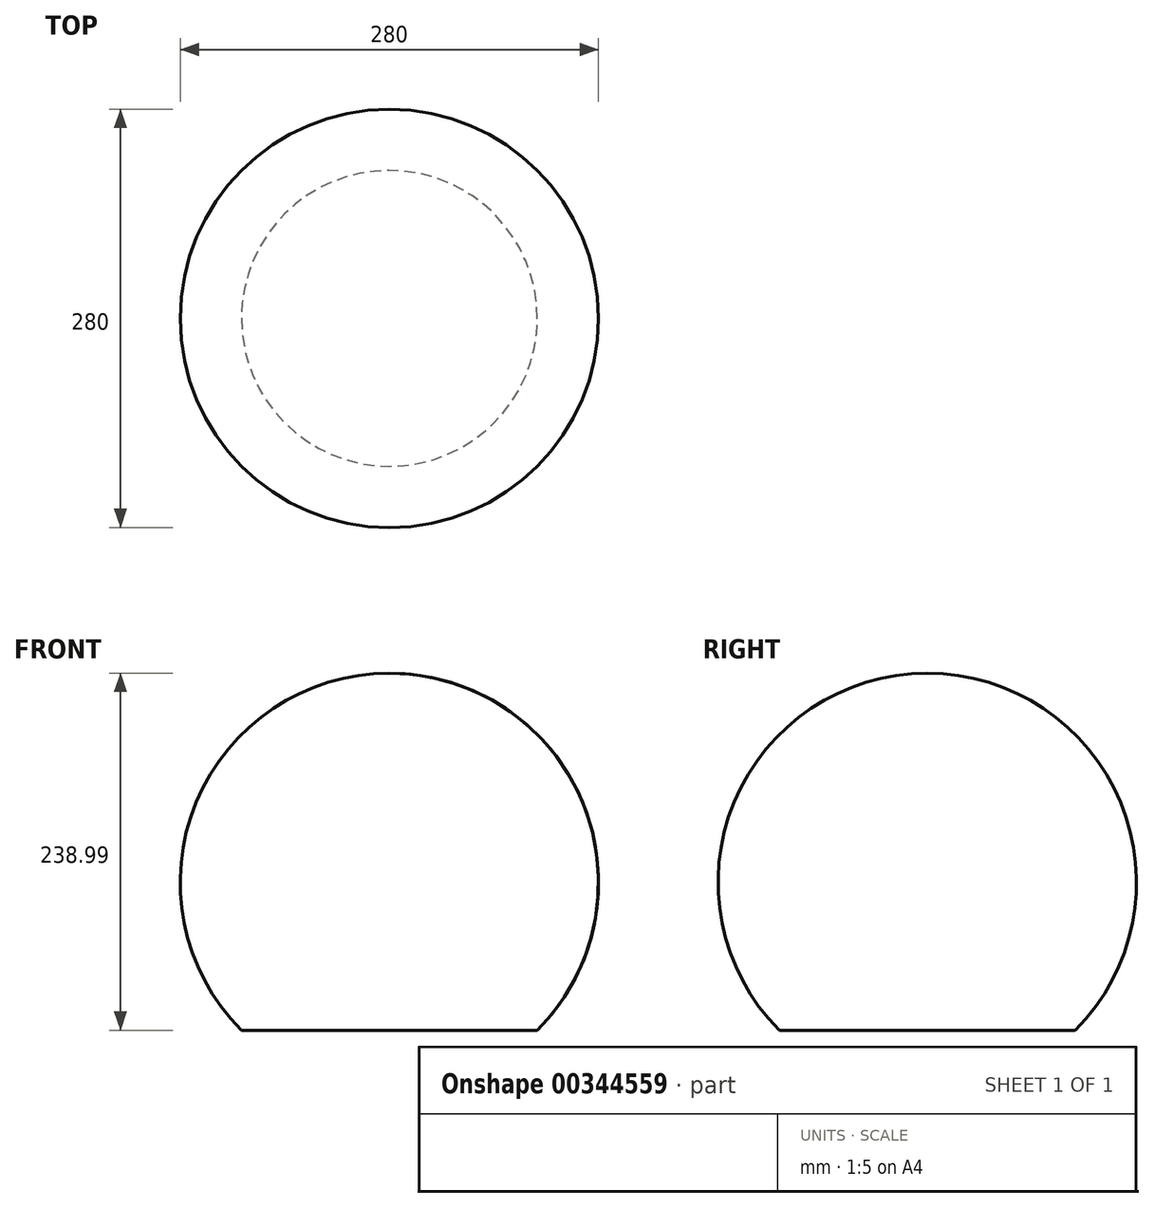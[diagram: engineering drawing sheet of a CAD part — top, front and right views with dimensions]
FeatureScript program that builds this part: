
annotation { "Feature Type Name" : "Feature", "Feature Type Description" : "" }
export const myFeature = defineFeature(function(context is Context, id is Id, definition is map)
    precondition{}
    {
        {
            var Q0;
            Q0=qCreatedBy(makeId("Top.planeOp"),FACE);
            var sketch = newSketch(context, id + "F0", { "sketchPlane" : qUnion([Q0])});
            skCircle(sketch, "E0", {"center": v(0, 0) * mm, "radius": 40.75 * mm});
            skLineSegment(sketch, "E1.bottom", {"start": v(6.25, -45.1) * mm, "end": v(-6.25, -45.1) * mm});
            skLineSegment(sketch, "E1.top", {"start": v(7.25, -40.1) * mm, "end": v(-7.25, -40.1) * mm});
            skLineSegment(sketch, "E1.left", {"start": v(7.25, -44.1) * mm, "end": v(7.25, -40.1) * mm});
            skLineSegment(sketch, "E1.right", {"start": v(-7.25, -44.1) * mm, "end": v(-7.25, -40.1) * mm});
            skPoint(sketch, "E1.middle", {"position": v(0, -42.6) * mm});
            skPoint(sketch, "E2.visualSharp", {"position": v(-7.25, -45.1) * mm});
            skArc(sketch, "E2.filletArc", {"start": v(-7.25, -44.1) * mm, "mid": v(-6.96, -44.8) * mm, "end": v(-6.25, -45.1) * mm});
            skPoint(sketch, "E3.visualSharp", {"position": v(7.25, -45.1) * mm});
            skArc(sketch, "E3.filletArc", {"start": v(6.25, -45.1) * mm, "mid": v(6.96, -44.8) * mm, "end": v(7.25, -44.1) * mm});
            skPoint(sketch, "E4.1.0", {"position": v(45.1, 7.25) * mm});
            skLineSegment(sketch, "E4.1.1", {"start": v(45.1, 6.25) * mm, "end": v(45.1, -6.25) * mm});
            skPoint(sketch, "E4.1.2", {"position": v(45.1, -7.25) * mm});
            skArc(sketch, "E4.1.3", {"start": v(44.1, -7.25) * mm, "mid": v(44.8, -6.96) * mm, "end": v(45.1, -6.25) * mm});
            skArc(sketch, "E4.1.4", {"start": v(45.1, 6.25) * mm, "mid": v(44.8, 6.96) * mm, "end": v(44.1, 7.25) * mm});
            skLineSegment(sketch, "E4.1.5", {"start": v(44.1, 7.25) * mm, "end": v(40.1, 7.25) * mm});
            skLineSegment(sketch, "E4.1.6", {"start": v(44.1, -7.25) * mm, "end": v(40.1, -7.25) * mm});
            skPoint(sketch, "E4.2.0", {"position": v(-7.25, 45.1) * mm});
            skLineSegment(sketch, "E4.2.1", {"start": v(-6.25, 45.1) * mm, "end": v(6.25, 45.1) * mm});
            skPoint(sketch, "E4.2.2", {"position": v(7.25, 45.1) * mm});
            skArc(sketch, "E4.2.3", {"start": v(7.25, 44.1) * mm, "mid": v(6.96, 44.8) * mm, "end": v(6.25, 45.1) * mm});
            skArc(sketch, "E4.2.4", {"start": v(-6.25, 45.1) * mm, "mid": v(-6.96, 44.8) * mm, "end": v(-7.25, 44.1) * mm});
            skLineSegment(sketch, "E4.2.5", {"start": v(-7.25, 44.1) * mm, "end": v(-7.25, 40.1) * mm});
            skLineSegment(sketch, "E4.2.6", {"start": v(7.25, 44.1) * mm, "end": v(7.25, 40.1) * mm});
            skPoint(sketch, "E4.3.0", {"position": v(-45.1, -7.25) * mm});
            skLineSegment(sketch, "E4.3.1", {"start": v(-45.1, -6.25) * mm, "end": v(-45.1, 6.25) * mm});
            skPoint(sketch, "E4.3.2", {"position": v(-45.1, 7.25) * mm});
            skArc(sketch, "E4.3.3", {"start": v(-44.1, 7.25) * mm, "mid": v(-44.8, 6.96) * mm, "end": v(-45.1, 6.25) * mm});
            skArc(sketch, "E4.3.4", {"start": v(-45.1, -6.25) * mm, "mid": v(-44.8, -6.96) * mm, "end": v(-44.1, -7.25) * mm});
            skLineSegment(sketch, "E4.3.5", {"start": v(-44.1, -7.25) * mm, "end": v(-40.1, -7.25) * mm});
            skLineSegment(sketch, "E4.3.6", {"start": v(-44.1, 7.25) * mm, "end": v(-40.1, 7.25) * mm});
            skSolve(sketch);
        }
        {
            var Q0;
            Q0=qCreatedBy(makeId("Front.planeOp"),FACE);
            var sketch = newSketch(context, id + "F1", { "sketchPlane" : qUnion([Q0])});
            skArc(sketch, "E5", {"start": v(99, 0) * mm, "mid": v(0, 239) * mm, "end": v(-99, 0) * mm});
            skLineSegment(sketch, "E6", {"start": v(-99, 0) * mm, "end": v(99, 0) * mm});
            skLineSegment(sketch, "E7", {"start": v(-99, 0) * mm, "end": v(-176.22, 77.22) * mm, "construction": true});
            skLineSegment(sketch, "E8", {"start": v(0, 0) * mm, "end": v(0, 239) * mm});
            skSolve(sketch);
        }
        {
            var Q0;
            {var subQ3=sQuery(id+"F1.wireOp",EDGE,"E8");Q0=makeQuery(id+"F1.imprint","IMPRINT",FACE,{"disambiguationData":[TD([[makeQuery(id+"F1.imprint","IMPRINT",EDGE,{"derivedFrom":subQ3}),-1.0]])]});}
            var Q1;
            Q1=sQuery(id+"F1.wireOp",EDGE,"E8");
            revolve(context, id + "F2", {"surfaceOperationType" : NewSurfaceOperationType.NEW, "entities" : qUnion([Q0]), "axis" : qUnion([Q1]), "revolveType" : RevolveType.FULL});
        }
    });
